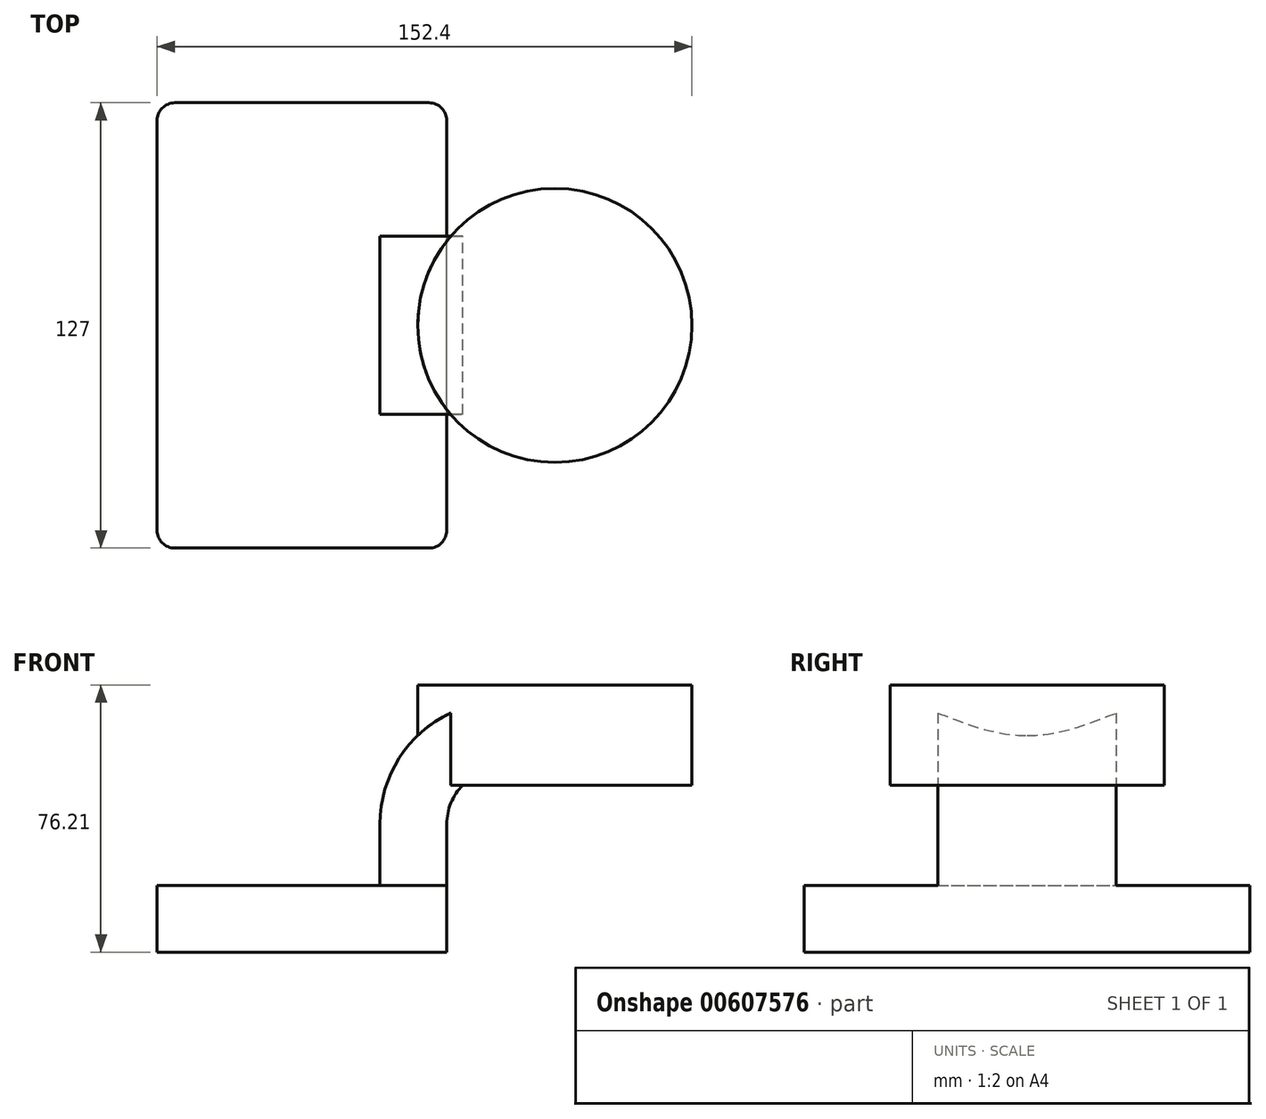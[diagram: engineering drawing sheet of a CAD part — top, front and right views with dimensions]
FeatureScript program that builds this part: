
annotation { "Feature Type Name" : "Feature", "Feature Type Description" : "" }
export const myFeature = defineFeature(function(context is Context, id is Id, definition is map)
    precondition{}
    {
        {
            var Q0;
            Q0=qCreatedBy(makeId("Front.planeOp"),FACE);
            var sketch = newSketch(context, id + "F0", { "sketchPlane" : qUnion([Q0])});
            skLineSegment(sketch, "E0.bottom", {"start": v(-41.28, -9.53) * mm, "end": v(41.28, -9.53) * mm});
            skLineSegment(sketch, "E0.top", {"start": v(-41.28, 9.53) * mm, "end": v(41.28, 9.53) * mm});
            skLineSegment(sketch, "E0.left", {"start": v(-41.28, -9.53) * mm, "end": v(-41.28, 9.53) * mm});
            skLineSegment(sketch, "E0.right", {"start": v(41.28, -9.53) * mm, "end": v(41.28, 9.52) * mm});
            skPoint(sketch, "E0.middle", {"position": v(0, 0) * mm});
            skLineSegment(sketch, "E1.bottom", {"start": v(60.32, 38.1) * mm, "end": v(111.12, 38.1) * mm});
            skLineSegment(sketch, "E1.top", {"start": v(60.32, 66.67) * mm, "end": v(111.12, 66.67) * mm});
            skLineSegment(sketch, "E1.left", {"start": v(60.32, 38.1) * mm, "end": v(60.32, 66.67) * mm});
            skLineSegment(sketch, "E1.right", {"start": v(111.12, 38.1) * mm, "end": v(111.12, 66.67) * mm});
            skPoint(sketch, "E1.middle", {"position": v(85.72, 52.39) * mm});
            skLineSegment(sketch, "E2", {"start": v(41.28, 9.52) * mm, "end": v(41.28, 27) * mm});
            skArc(sketch, "E3", {"start": v(41.27, 27) * mm, "mid": v(45.92, 38.23) * mm, "end": v(57.15, 42.88) * mm});
            skLineSegment(sketch, "E4", {"start": v(57.15, 42.88) * mm, "end": v(71.81, 42.88) * mm});
            skLineSegment(sketch, "E5.0", {"start": v(57.15, 61.93) * mm, "end": v(71.81, 61.93) * mm});
            skArc(sketch, "E5.1", {"start": v(22.23, 27) * mm, "mid": v(32.45, 51.7) * mm, "end": v(57.15, 61.93) * mm});
            skLineSegment(sketch, "E5.2", {"start": v(22.22, 9.52) * mm, "end": v(22.22, 27) * mm});
            skLineSegment(sketch, "E6", {"start": v(72.07, 38.1) * mm, "end": v(72.07, 66.67) * mm});
            skFitSpline(sketch, "E7", {"points": [v(-41.28, 9.52) * mm, v(57.15, 61.93) * mm], "startDerivative": vector(1.32, 71.43) * mm, "endDerivative": vector(103.1, -2.78) * mm});
            skSolve(sketch);
        }
        {
            var Q0;
            Q0=makeQuery(id+"F0.imprint","IMPRINT",FACE,{"disambiguationData":[TD([[makeQuery(id+"F0.imprint","IMPRINT",EDGE,{"derivedFrom":sQuery(id+"F0.wireOp",EDGE,"E0.bottom")}),1.0]])]});
            extrude(context, id + "F1", {"entities" : qUnion([Q0]), "endBound" : BoundingType.SYMMETRIC, "depth" : 127 * mm, "offsetDistance" : 25.4 * mm});
        }
        {
            var Q0;
            {var subQ1=sQuery(id+"F0.wireOp",EDGE,"E2");Q0=makeQuery(id+"F0.imprint","IMPRINT",FACE,{"disambiguationData":[TD([[makeQuery(id+"F0.imprint","IMPRINT",EDGE,{"derivedFrom":subQ1}),1.0]])]});}
            var Q1;
            {var subQ6=sQuery(id+"F0.wireOp",EDGE,"E6");Q1=makeQuery(id+"F0.imprint","IMPRINT",FACE,{"disambiguationData":[TD([[makeQuery(id+"F0.imprint","IMPRINT",EDGE,{"derivedFrom":subQ6}),1.0]])]});}
            extrude(context, id + "F2", {"entities" : qUnion([Q0, Q1]), "operationType" : NewBodyOperationType.ADD, "endBound" : BoundingType.SYMMETRIC, "depth" : 50.8 * mm, "offsetDistance" : 25.4 * mm});
        }
        {
            var Q0;
            Q0=makeQuery(id+"F0.imprint","IMPRINT",FACE,{"disambiguationData":[TD([[makeQuery(id+"F0.imprint","IMPRINT",EDGE,{"derivedFrom":sQuery(id+"F0.wireOp",EDGE,"E5.1")}),1.0]])]});
            extrude(context, id + "F3", {"entities" : qUnion([Q0]), "operationType" : NewBodyOperationType.ADD, "endBound" : BoundingType.SYMMETRIC, "depth" : 15.88 * mm, "offsetDistance" : 25.4 * mm});
        }
        {
            var Q0;
            {var subQ0=sQuery(id+"F0.wireOp",EDGE,"E1.right");Q0=makeQuery(id+"F0.imprint","IMPRINT",FACE,{"disambiguationData":[TD([[makeQuery(id+"F0.imprint","IMPRINT",EDGE,{"derivedFrom":subQ0}),1.0]])]});}
            var Q1;
            Q1=sQuery(id+"F0.wireOp",EDGE,"E6");
            revolve(context, id + "F4", {"operationType" : NewBodyOperationType.ADD, "entities" : qUnion([Q0]), "axis" : qUnion([Q1]), "revolveType" : RevolveType.FULL});
        }
        {
            var Q0;
            Q0=makeQuery(id+"F1.opExtrude","CAP_EDGE",EDGE,{"disambiguationData":[OSD([sQuery(id+"F0.wireOp",EDGE,"E0.right")])],"isStart":false});
            var Q1;
            Q1=makeQuery(id+"F1.opExtrude","CAP_EDGE",EDGE,{"disambiguationData":[OSD([sQuery(id+"F0.wireOp",EDGE,"E0.right")])],"isStart":true});
            var Q2;
            Q2=makeQuery(id+"F1.opExtrude","CAP_EDGE",EDGE,{"disambiguationData":[OSD([sQuery(id+"F0.wireOp",EDGE,"E0.left")])],"isStart":true});
            var Q3;
            Q3=makeQuery(id+"F1.opExtrude","CAP_EDGE",EDGE,{"disambiguationData":[OSD([sQuery(id+"F0.wireOp",EDGE,"E0.left")])],"isStart":false});
            fillet(context, id + "F5", {"entities" : qUnion([Q0, Q1, Q2, Q3]), "radius" : 5.08 * mm, "tangentPropagation" : true, "allowEdgeOverflow" : false});
        }
    });
